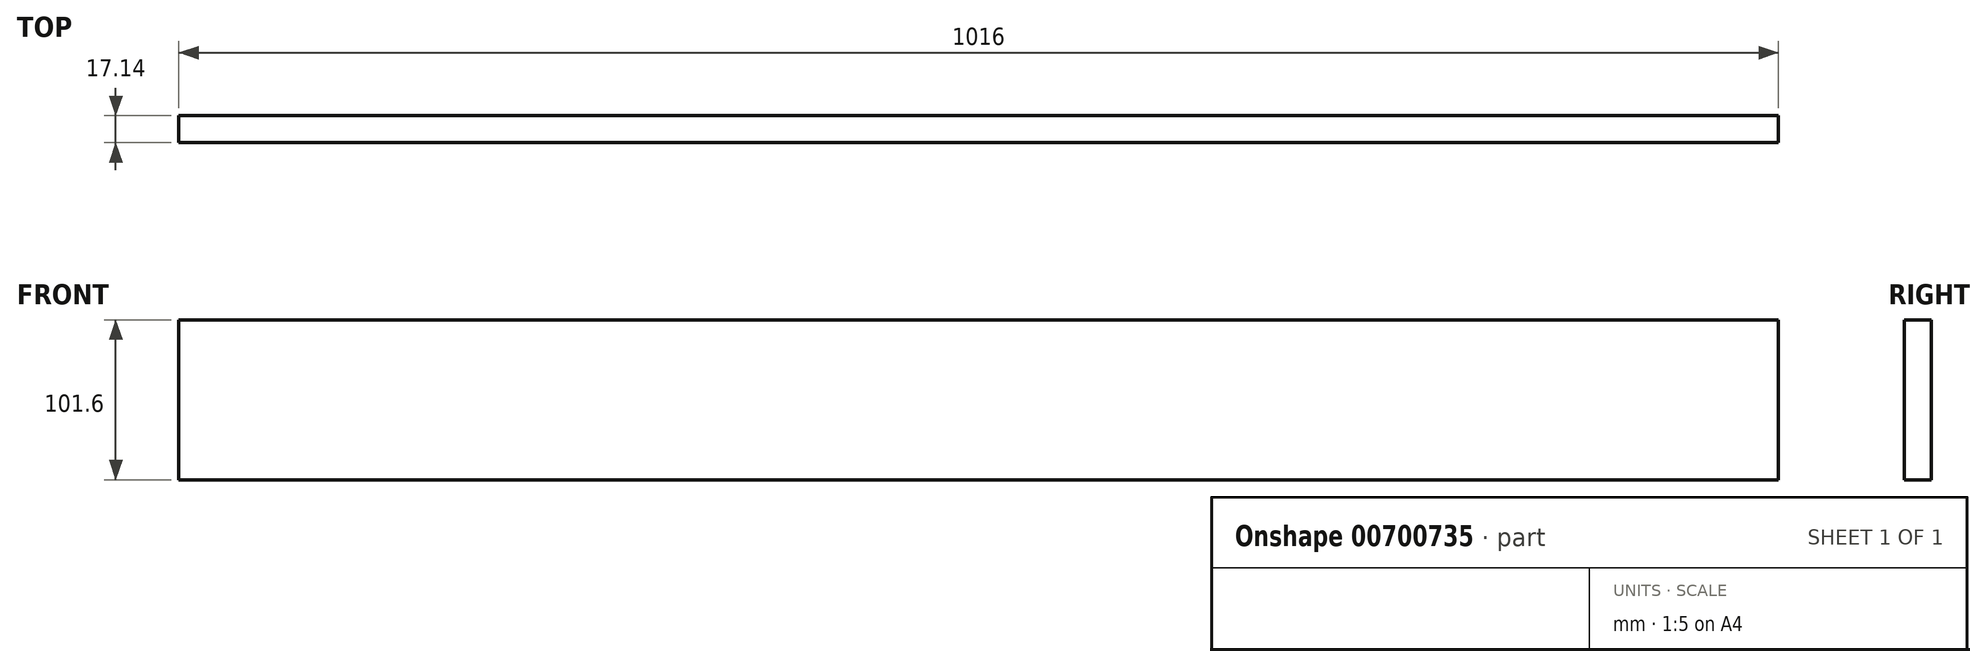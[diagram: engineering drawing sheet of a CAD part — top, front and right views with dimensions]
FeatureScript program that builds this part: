
annotation { "Feature Type Name" : "Feature", "Feature Type Description" : "" }
export const myFeature = defineFeature(function(context is Context, id is Id, definition is map)
    precondition{}
    {
        {
            var Q0;
            Q0=qCreatedBy(makeId("Front.planeOp"),FACE);
            var sketch = newSketch(context, id + "F0", { "sketchPlane" : qUnion([Q0])});
            skLineSegment(sketch, "E0.bottom", {"start": v(0, 0) * mm, "end": v(1016, 0) * mm});
            skLineSegment(sketch, "E0.top", {"start": v(0, 101.6) * mm, "end": v(1016, 101.6) * mm});
            skLineSegment(sketch, "E0.left", {"start": v(0, 0) * mm, "end": v(0, 101.6) * mm});
            skLineSegment(sketch, "E0.right", {"start": v(1016, 0) * mm, "end": v(1016, 101.6) * mm});
            skSolve(sketch);
        }
        {
            var Q0;
            Q0 = qSketchRegion(id + "F0", true);
            extrude(context, id + "F1", {"entities" : qUnion([Q0]), "depth" : 17.14 * mm, "offsetDistance" : 25.4 * mm});
        }
    });
